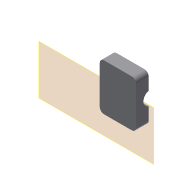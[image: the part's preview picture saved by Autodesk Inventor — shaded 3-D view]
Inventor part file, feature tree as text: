
AUTODESK INVENTOR PART (.ipt)
format: ipt  version: 2022 (Build 260153000, 153)  size: 131,072 bytes
history: native  units: mm
features: reference x5, extrude x3, sketch x3, other x3, plane x1, fillet x1, projected_geometry x1
ambient origin geometry x8: Origin, YZ Plane, XZ Plane, XY Plane, X Axis, Y Axis, Z Axis, Center Point
bodies: Volumenkörper1 (feature_tree)
feature tree (17):
  plane  "Arbeitsebene1"
  extrude  "Extrusion1"  Depth=5.0mm
  extrude  "Extrusion2"  Depth=5.0mm
  extrude  "Extrusion3"  Depth=4.0mm TaperAngle=0.0deg
  fillet  "Rundung1"  Radius=2.0mm
  sketch  "Skizze1"  dims[d0=3.6mm d1=5.0mm]
  reference  "Referenz1"
  reference  "Referenz2"
  reference  "Referenz3"
  reference  "Referenz4"
  sketch  "Skizze2"  dims[d2=5.0mm d3=5.0mm]
  projected_geometry  "Projizierte Kontur1"
  sketch  "Skizze3"  dims[d4=5.0mm d5=4.0mm d6=0.0mm d7=2.0mm d8=0.0mm d9=6.44mm d10=6.44mm d11=0.0mm d12=0.0mm d13=2.0mm]
  reference  "Referenz5"
  other  "Assembly_Cube_Syringepump_Micro_v3.iam"
  other  "20_Cube_Insert_Template_v3:1"
  other  "00_Syringe_10ml:1"
